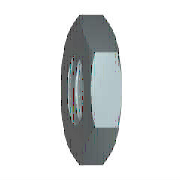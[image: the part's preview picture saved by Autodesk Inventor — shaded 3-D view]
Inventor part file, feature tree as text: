
AUTODESK INVENTOR PART (.ipt)
format: ipt  version: 2015 (Build 190159000, 159)  size: 171,520 bytes
history: native  units: mm (DEFAULTED — no unit token found)
features: sketch x3, chamfer x1, hole x1, other x1, plane x1
ambient origin geometry x7: Origin, YZ Plane, XZ Plane, X Axis, Y Axis, Z Axis, Center Point
bodies: Solid1 (feature_tree), Body (feature_tree)
feature tree (7):
  chamfer  "Chamfer1"  Angle=30.0deg  [1 undecoded]
  hole  "Thread"  [1 undecoded]
  other  "Work Axis1"
  plane  "Work Plane1"
  sketch  "Sketch1"  dims[d0=9.150771mm]
  sketch  "Sketch2"  dims[d1=2.8956mm]
  sketch  "Sketch3"  dims[d2=0.0mm d3=30.0deg d4=30.0deg d5=7.9248mm d6=7.9248mm d7=90.0deg d25=2.6416mm d26=6.0mm d27=4.0mm d28=2.0mm d29=14.3117mm d30=8.0mm d31=20.594885mm d8=0.42963mm d9=30.0deg d10=0.42963mm d11=30.0deg d13=0.0mm d14=0.0mm d39=0.0mm d40=0.42963mm d41=0.42963mm d42=0.0mm]
note: 2 required parameter values undecoded (feature->parameter linkage not recoverable at this tier; creation-order binding heuristic only, values carry confidence <= 0.55)
